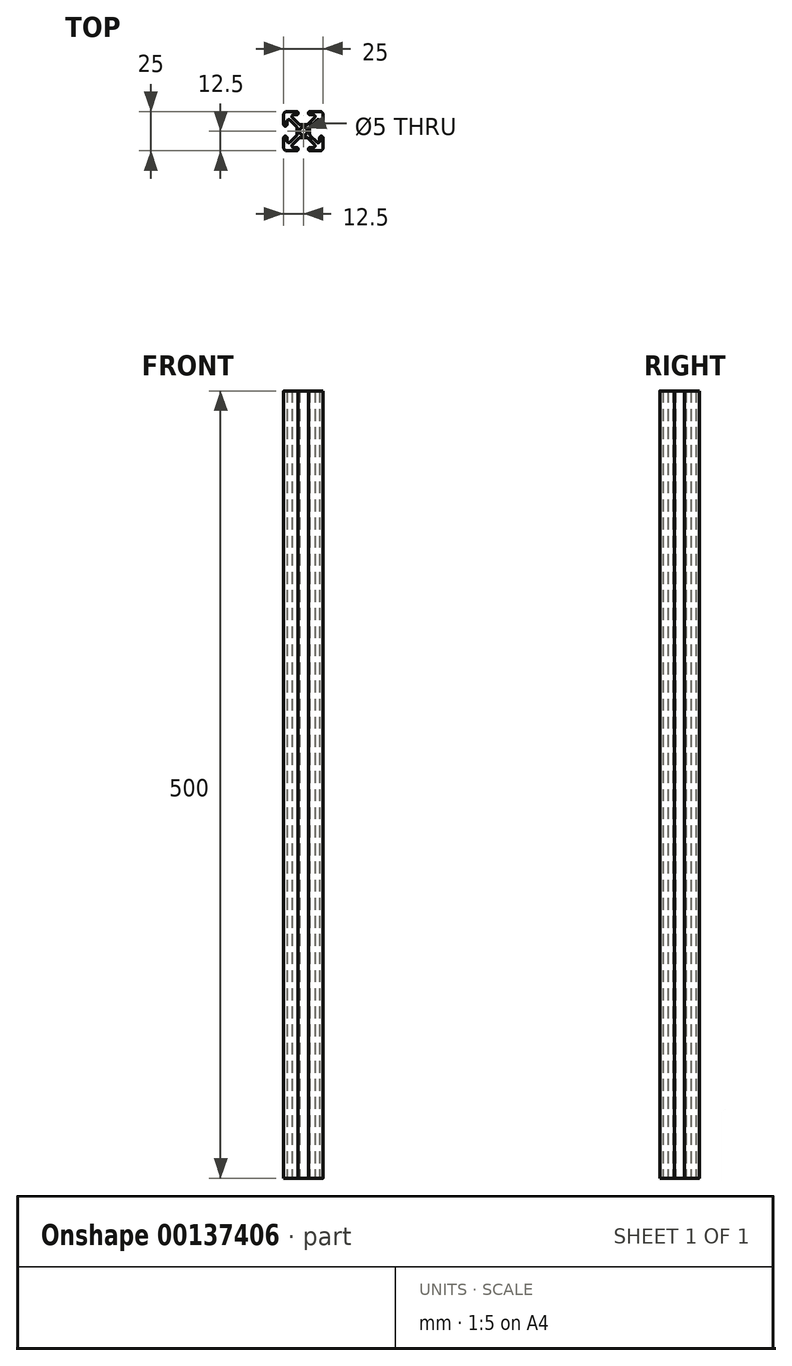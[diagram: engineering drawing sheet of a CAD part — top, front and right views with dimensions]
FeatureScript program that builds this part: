
annotation { "Feature Type Name" : "Feature", "Feature Type Description" : "" }
export const myFeature = defineFeature(function(context is Context, id is Id, definition is map)
    precondition{}
    {
        {
            var Q0;
            Q0=qCreatedBy(makeId("Top.planeOp"),FACE);
            var sketch = newSketch(context, id + "F0", { "sketchPlane" : qUnion([Q0])});
            skCircle(sketch, "E0", {"center": v(0, 0) * mm, "radius": 2.5 * mm});
            skLineSegment(sketch, "E1", {"start": v(0, 0) * mm, "end": v(0, 4.05) * mm, "construction": true});
            skLineSegment(sketch, "E2", {"start": v(0, 0) * mm, "end": v(-4.05, 0) * mm, "construction": true});
            skLineSegment(sketch, "E3", {"start": v(0, 0) * mm, "end": v(-12.5, 12.5) * mm, "construction": true});
            skLineSegment(sketch, "E4", {"start": v(-12.5, 10.36) * mm, "end": v(-12.5, 4.32) * mm});
            skLineSegment(sketch, "E5", {"start": v(-10.36, 12.5) * mm, "end": v(-4.32, 12.5) * mm});
            skLineSegment(sketch, "E6", {"start": v(-4.32, 10.36) * mm, "end": v(-6.26, 10.36) * mm});
            skLineSegment(sketch, "E7", {"start": v(-10.36, 6.26) * mm, "end": v(-10.36, 4.32) * mm});
            skArc(sketch, "E8", {"start": v(-4.32, 12.5) * mm, "mid": v(-3.25, 11.43) * mm, "end": v(-4.32, 10.36) * mm});
            skArc(sketch, "E9", {"start": v(-10.36, 4.32) * mm, "mid": v(-11.43, 3.25) * mm, "end": v(-12.5, 4.32) * mm});
            skLineSegment(sketch, "E10", {"start": v(0, 4.05) * mm, "end": v(-2.1, 4.05) * mm});
            skLineSegment(sketch, "E11", {"start": v(-4.05, 2.1) * mm, "end": v(-4.05, 0) * mm});
            skLineSegment(sketch, "E12", {"start": v(-8.53, 7.02) * mm, "end": v(-4.36, 2.85) * mm});
            skLineSegment(sketch, "E13", {"start": v(-7.02, 8.53) * mm, "end": v(-2.85, 4.36) * mm});
            skLineSegment(sketch, "E14.0.MirrorCS", {"start": v(10.36, 6.26) * mm, "end": v(10.36, 4.32) * mm});
            skLineSegment(sketch, "E14.1.MirrorCS", {"start": v(7.02, 8.53) * mm, "end": v(2.85, 4.36) * mm});
            skArc(sketch, "E14.2.MirrorCS", {"start": v(4.32, 12.5) * mm, "mid": v(3.25, 11.43) * mm, "end": v(4.32, 10.36) * mm});
            skArc(sketch, "E14.3.MirrorCS", {"start": v(10.36, 4.32) * mm, "mid": v(11.43, 3.25) * mm, "end": v(12.5, 4.32) * mm});
            skLineSegment(sketch, "E14.4.MirrorCS", {"start": v(10.36, 12.5) * mm, "end": v(4.32, 12.5) * mm});
            skLineSegment(sketch, "E14.5.MirrorCS", {"start": v(4.32, 10.36) * mm, "end": v(6.26, 10.36) * mm});
            skLineSegment(sketch, "E14.6.MirrorCS", {"start": v(12.5, 10.36) * mm, "end": v(12.5, 4.32) * mm});
            skLineSegment(sketch, "E14.7.MirrorCS", {"start": v(8.53, 7.02) * mm, "end": v(4.36, 2.85) * mm});
            skLineSegment(sketch, "E15.0.MirrorCS", {"start": v(0, 4.05) * mm, "end": v(2.1, 4.05) * mm});
            skLineSegment(sketch, "E16.0.MirrorCS", {"start": v(4.05, 2.1) * mm, "end": v(4.05, 0) * mm});
            skLineSegment(sketch, "E17.0.MirrorCS", {"start": v(10.36, -12.5) * mm, "end": v(4.32, -12.5) * mm});
            skLineSegment(sketch, "E17.1.MirrorCS", {"start": v(12.5, -10.36) * mm, "end": v(12.5, -4.32) * mm});
            skArc(sketch, "E17.2.MirrorCS", {"start": v(4.32, -12.5) * mm, "mid": v(3.25, -11.43) * mm, "end": v(4.32, -10.36) * mm});
            skLineSegment(sketch, "E17.3.MirrorCS", {"start": v(-7.02, -8.53) * mm, "end": v(-2.85, -4.36) * mm});
            skLineSegment(sketch, "E17.4.MirrorCS", {"start": v(7.02, -8.53) * mm, "end": v(2.85, -4.36) * mm});
            skLineSegment(sketch, "E17.5.MirrorCS", {"start": v(10.36, -6.26) * mm, "end": v(10.36, -4.32) * mm});
            skLineSegment(sketch, "E17.6.MirrorCS", {"start": v(8.53, -7.02) * mm, "end": v(4.36, -2.85) * mm});
            skLineSegment(sketch, "E17.7.MirrorCS", {"start": v(-10.36, -12.5) * mm, "end": v(-4.32, -12.5) * mm});
            skLineSegment(sketch, "E17.8.MirrorCS", {"start": v(-4.32, -10.36) * mm, "end": v(-6.26, -10.36) * mm});
            skLineSegment(sketch, "E17.9.MirrorCS", {"start": v(4.32, -10.36) * mm, "end": v(6.26, -10.36) * mm});
            skArc(sketch, "E17.10.MirrorCS", {"start": v(10.36, -4.32) * mm, "mid": v(11.43, -3.25) * mm, "end": v(12.5, -4.32) * mm});
            skLineSegment(sketch, "E17.11.MirrorCS", {"start": v(-12.5, -10.36) * mm, "end": v(-12.5, -4.32) * mm});
            skLineSegment(sketch, "E17.12.MirrorCS", {"start": v(0, -4.05) * mm, "end": v(2.1, -4.05) * mm});
            skArc(sketch, "E17.13.MirrorCS", {"start": v(-4.32, -12.5) * mm, "mid": v(-3.25, -11.43) * mm, "end": v(-4.32, -10.36) * mm});
            skLineSegment(sketch, "E17.14.MirrorCS", {"start": v(-8.53, -7.02) * mm, "end": v(-4.36, -2.85) * mm});
            skArc(sketch, "E17.15.MirrorCS", {"start": v(-10.36, -4.32) * mm, "mid": v(-11.43, -3.25) * mm, "end": v(-12.5, -4.32) * mm});
            skLineSegment(sketch, "E17.16.MirrorCS", {"start": v(-10.36, -6.26) * mm, "end": v(-10.36, -4.32) * mm});
            skLineSegment(sketch, "E17.17.MirrorCS", {"start": v(0, -4.05) * mm, "end": v(-2.1, -4.05) * mm});
            skLineSegment(sketch, "E18.0.MirrorCS", {"start": v(4.05, -2.1) * mm, "end": v(4.05, 0) * mm});
            skLineSegment(sketch, "E19.0.MirrorCS", {"start": v(-4.05, -2.1) * mm, "end": v(-4.05, 0) * mm});
            skPoint(sketch, "E20.visualSharp", {"position": v(-12.5, 12.5) * mm});
            skArc(sketch, "E20.filletArc", {"start": v(-10.36, 12.5) * mm, "mid": v(-11.87, 11.87) * mm, "end": v(-12.5, 10.36) * mm});
            skPoint(sketch, "E21.visualSharp", {"position": v(12.5, 12.5) * mm});
            skArc(sketch, "E21.filletArc", {"start": v(12.5, 10.36) * mm, "mid": v(11.87, 11.87) * mm, "end": v(10.36, 12.5) * mm});
            skPoint(sketch, "E22.visualSharp", {"position": v(12.5, -12.5) * mm});
            skArc(sketch, "E22.filletArc", {"start": v(10.36, -12.5) * mm, "mid": v(11.87, -11.87) * mm, "end": v(12.5, -10.36) * mm});
            skPoint(sketch, "E23.visualSharp", {"position": v(-12.5, -12.5) * mm});
            skArc(sketch, "E23.filletArc", {"start": v(-12.5, -10.36) * mm, "mid": v(-11.87, -11.87) * mm, "end": v(-10.36, -12.5) * mm});
            skPoint(sketch, "E24.visualSharp", {"position": v(4.05, 4.05) * mm});
            skPoint(sketch, "E25.visualSharp", {"position": v(-10.36, 8.85) * mm});
            skArc(sketch, "E25.filletArc", {"start": v(-8.53, 7.02) * mm, "mid": v(-9.7, 7.25) * mm, "end": v(-10.36, 6.26) * mm});
            skPoint(sketch, "E26.visualSharp", {"position": v(-8.85, 10.36) * mm});
            skArc(sketch, "E26.filletArc", {"start": v(-6.26, 10.36) * mm, "mid": v(-7.25, 9.7) * mm, "end": v(-7.02, 8.53) * mm});
            skPoint(sketch, "E27.visualSharp", {"position": v(8.85, 10.36) * mm});
            skArc(sketch, "E27.filletArc", {"start": v(7.02, 8.53) * mm, "mid": v(7.25, 9.7) * mm, "end": v(6.26, 10.36) * mm});
            skPoint(sketch, "E28.visualSharp", {"position": v(10.36, 8.85) * mm});
            skArc(sketch, "E28.filletArc", {"start": v(10.36, 6.26) * mm, "mid": v(9.7, 7.25) * mm, "end": v(8.53, 7.02) * mm});
            skPoint(sketch, "E29.visualSharp", {"position": v(10.36, -8.85) * mm});
            skArc(sketch, "E29.filletArc", {"start": v(8.53, -7.02) * mm, "mid": v(9.7, -7.25) * mm, "end": v(10.36, -6.26) * mm});
            skPoint(sketch, "E30.visualSharp", {"position": v(8.85, -10.36) * mm});
            skArc(sketch, "E30.filletArc", {"start": v(6.26, -10.36) * mm, "mid": v(7.25, -9.7) * mm, "end": v(7.02, -8.53) * mm});
            skPoint(sketch, "E31.visualSharp", {"position": v(-8.85, -10.36) * mm});
            skArc(sketch, "E31.filletArc", {"start": v(-7.02, -8.53) * mm, "mid": v(-7.25, -9.7) * mm, "end": v(-6.26, -10.36) * mm});
            skPoint(sketch, "E32.visualSharp", {"position": v(-10.36, -8.85) * mm});
            skArc(sketch, "E32.filletArc", {"start": v(-10.36, -6.26) * mm, "mid": v(-9.7, -7.25) * mm, "end": v(-8.53, -7.02) * mm});
            skPoint(sketch, "E33.orphan", {"position": v(-4.05, 4.05) * mm});
            skPoint(sketch, "E34.orphan", {"position": v(4.05, -4.05) * mm});
            skPoint(sketch, "E35.orphan", {"position": v(-4.05, -4.05) * mm});
            skPoint(sketch, "E36.visualSharp", {"position": v(-2.54, 4.05) * mm});
            skArc(sketch, "E36.filletArc", {"start": v(-2.85, 4.36) * mm, "mid": v(-2.5, 4.13) * mm, "end": v(-2.1, 4.05) * mm});
            skPoint(sketch, "E37.visualSharp", {"position": v(2.54, 4.05) * mm});
            skArc(sketch, "E37.filletArc", {"start": v(2.1, 4.05) * mm, "mid": v(2.5, 4.13) * mm, "end": v(2.85, 4.36) * mm});
            skPoint(sketch, "E38.visualSharp", {"position": v(-4.05, 2.54) * mm});
            skArc(sketch, "E38.filletArc", {"start": v(-4.05, 2.1) * mm, "mid": v(-4.13, 2.5) * mm, "end": v(-4.36, 2.85) * mm});
            skPoint(sketch, "E39.visualSharp", {"position": v(-4.05, -2.54) * mm});
            skArc(sketch, "E39.filletArc", {"start": v(-4.36, -2.85) * mm, "mid": v(-4.13, -2.5) * mm, "end": v(-4.05, -2.1) * mm});
            skPoint(sketch, "E40.visualSharp", {"position": v(-2.54, -4.05) * mm});
            skArc(sketch, "E40.filletArc", {"start": v(-2.1, -4.05) * mm, "mid": v(-2.5, -4.13) * mm, "end": v(-2.85, -4.36) * mm});
            skPoint(sketch, "E41.visualSharp", {"position": v(2.54, -4.05) * mm});
            skArc(sketch, "E41.filletArc", {"start": v(2.85, -4.36) * mm, "mid": v(2.5, -4.13) * mm, "end": v(2.1, -4.05) * mm});
            skPoint(sketch, "E42.visualSharp", {"position": v(4.05, -2.54) * mm});
            skArc(sketch, "E42.filletArc", {"start": v(4.05, -2.1) * mm, "mid": v(4.13, -2.5) * mm, "end": v(4.36, -2.85) * mm});
            skPoint(sketch, "E43.visualSharp", {"position": v(4.05, 2.54) * mm});
            skArc(sketch, "E43.filletArc", {"start": v(4.36, 2.85) * mm, "mid": v(4.13, 2.5) * mm, "end": v(4.05, 2.1) * mm});
            skSolve(sketch);
        }
        {
            var Q0;
            Q0=qSketchRegion(id+"F0",true);
            extrude(context, id + "F1", {"entities" : qUnion([Q0]), "depth" : 500 * mm});
        }
    });
